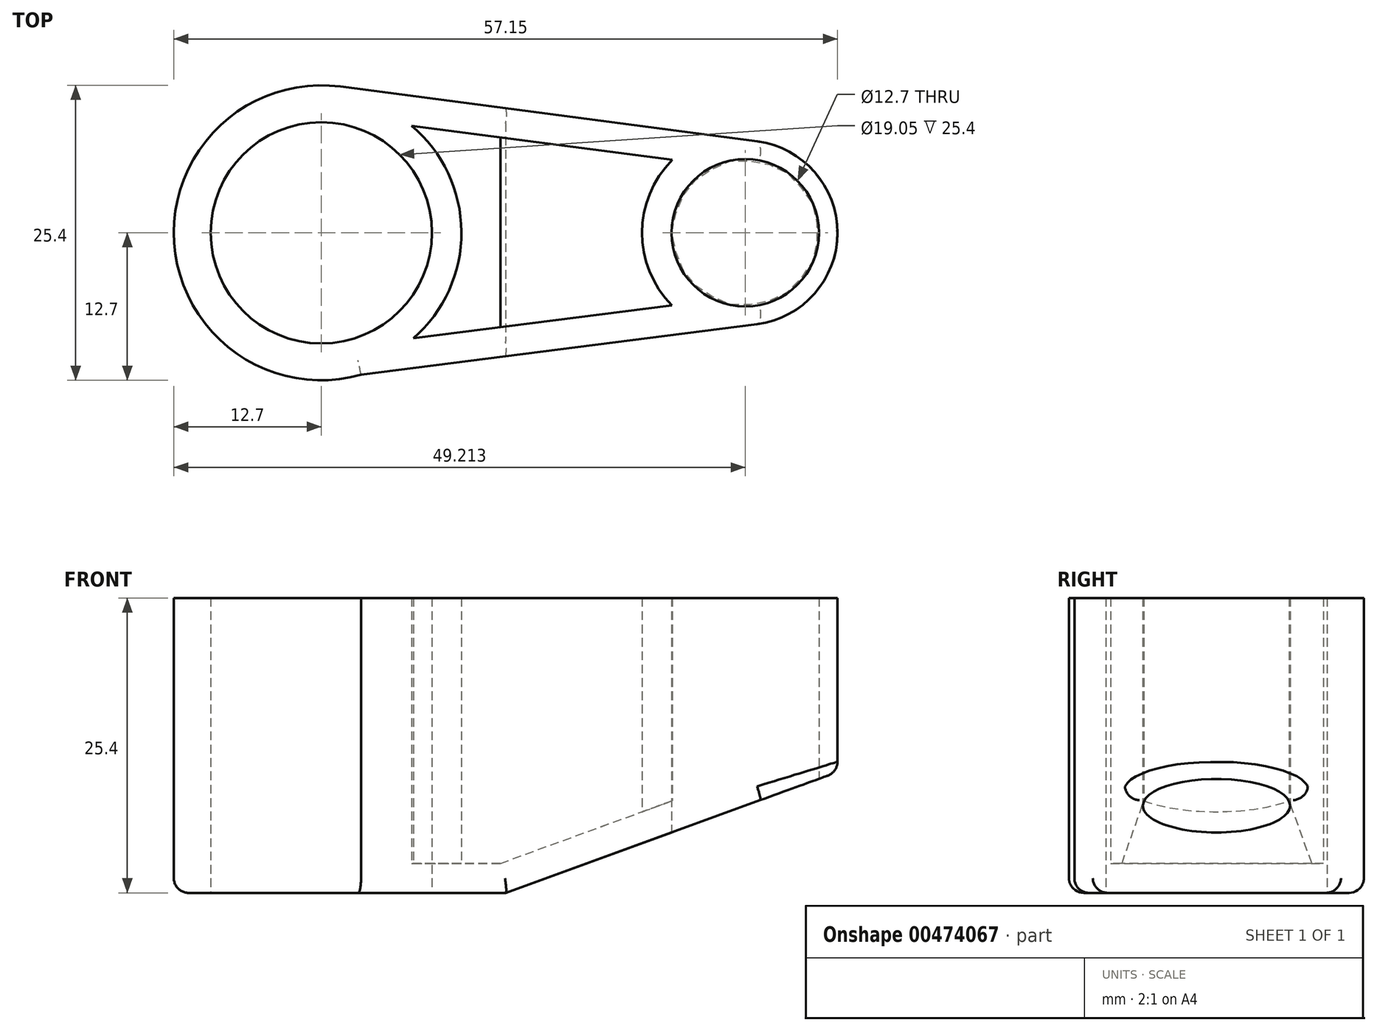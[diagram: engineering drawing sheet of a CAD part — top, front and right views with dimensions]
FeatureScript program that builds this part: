
annotation { "Feature Type Name" : "Feature", "Feature Type Description" : "" }
export const myFeature = defineFeature(function(context is Context, id is Id, definition is map)
    precondition{}
    {
        {
            var Q0;
            Q0=qCreatedBy(makeId("Top.planeOp"),FACE);
            var sketch = newSketch(context, id + "F0", { "sketchPlane" : qUnion([Q0])});
            skCircle(sketch, "E0", {"center": v(0, 0) * mm, "radius": 12.7 * mm});
            skCircle(sketch, "E1", {"center": v(36.51, 0) * mm, "radius": 7.94 * mm});
            skCircle(sketch, "E2", {"center": v(0, 0) * mm, "radius": 9.53 * mm});
            skCircle(sketch, "E3", {"center": v(36.51, 0) * mm, "radius": 6.35 * mm});
            skLineSegment(sketch, "E4", {"start": v(3.42, -12.23) * mm, "end": v(37.52, -7.87) * mm});
            skLineSegment(sketch, "E5", {"start": v(1.66, 12.6) * mm, "end": v(37.55, 7.87) * mm});
            skSolve(sketch);
        }
        {
            var Q0;
            {var subQ0=sQuery(id+"F0.wireOp",EDGE,"E4");Q0=makeQuery(id+"F0.imprint","IMPRINT",FACE,{"disambiguationData":[TD([[makeQuery(id+"F0.imprint","IMPRINT",EDGE,{"derivedFrom":subQ0}),1.0]])]});}
            var Q1;
            Q1=makeQuery(id+"F0.imprint","IMPRINT",FACE,{"disambiguationData":[TD([[makeQuery(id+"F0.imprint","IMPRINT",EDGE,{"derivedFrom":sQuery(id+"F0.wireOp",EDGE,"E2")}),-1.0]])]});
            var Q2;
            Q2=makeQuery(id+"F0.imprint","IMPRINT",FACE,{"disambiguationData":[TD([[makeQuery(id+"F0.imprint","IMPRINT",EDGE,{"derivedFrom":sQuery(id+"F0.wireOp",EDGE,"E3")}),-1.0]])]});
            extrude(context, id + "F1", {"entities" : qUnion([Q0, Q1, Q2]), "depth" : 25.4 * mm, "offsetDistance" : 25.4 * mm});
        }
        {
            var Q0;
            Q0=qCreatedBy(makeId("Front.planeOp"),FACE);
            var sketch = newSketch(context, id + "F2", { "sketchPlane" : qUnion([Q0])});
            skLineSegment(sketch, "E6", {"start": v(15.87, 0) * mm, "end": v(44.45, 10.4) * mm});
            skLineSegment(sketch, "E7", {"start": v(44.45, 10.4) * mm, "end": v(44.45, 0) * mm});
            skLineSegment(sketch, "E8", {"start": v(44.45, 0) * mm, "end": v(15.88, 0) * mm});
            skLineSegment(sketch, "E9", {"start": v(44.45, 25.4) * mm, "end": v(44.45, 0) * mm});
            skSolve(sketch);
        }
        {
            var Q0;
            Q0=makeQuery(id+"F2.imprint","IMPRINT",FACE,{"disambiguationData":[TD([[makeQuery(id+"F2.imprint","IMPRINT",EDGE,{"derivedFrom":sQuery(id+"F2.wireOp",EDGE,"E6")}),-1.0]])]});
            extrude(context, id + "F3", {"entities" : qUnion([Q0]), "operationType" : NewBodyOperationType.REMOVE, "oppositeDirection" : true, "depth" : 25.4 * mm, "offsetDistance" : 25.4 * mm, "hasSecondDirection" : true, "secondDirectionOppositeDirection" : false, "secondDirectionDepth" : 25.4 * mm});
        }
        {
            var Q0;
            Q0=makeQuery(id+"F3.boolean.opBoolean","INTERSECT",EDGE,{"derivedFrom":[makeQuery(id+"F1.opExtrude","SWEPT_FACE",FACE,{"disambiguationData":[OSD([sQuery(id+"F0.wireOp",EDGE,"E5")])]}),makeQuery(id+"F3.opExtrude","SWEPT_FACE",FACE,{"disambiguationData":[OSD([sQuery(id+"F2.wireOp",EDGE,"E6")])]})]});
            var Q1;
            Q1=makeQuery(id+"F1.opExtrude","CAP_EDGE",EDGE,{"disambiguationData":[OSD([sQuery(id+"F0.wireOp",EDGE,"E0")])],"isStart":true});
            var Q2;
            Q2=makeQuery(id+"F1.opExtrude","CAP_EDGE",EDGE,{"disambiguationData":[OSD([sQuery(id+"F0.wireOp",EDGE,"E5")])],"isStart":true});
            var Q3;
            Q3=makeQuery(id+"F1.opExtrude","CAP_EDGE",EDGE,{"disambiguationData":[OSD([sQuery(id+"F0.wireOp",EDGE,"E4")])],"isStart":true});
            var Q4;
            Q4=makeQuery(id+"F3.boolean.opBoolean","COPY",EDGE,{"derivedFrom":makeQuery(id+"F3.opExtrude","SWEPT_EDGE",EDGE,{"disambiguationData":[OSD([sQuery(id+"F2.wireOp",EDGE,"E6"),sQuery(id+"F2.wireOp",EDGE,"E8")])]})});
            fillet(context, id + "F4", {"entities" : qUnion([Q0, Q1, Q2, Q3, Q4]), "radius" : 1.27 * mm, "tangentPropagation" : true, "allowEdgeOverflow" : false});
        }
        {
            var Q0;
            Q0=makeQuery(id+"F1.opExtrude","CAP_FACE",FACE,{"disambiguationData":[OSD([sQuery(id+"F0.wireOp",EDGE,"E0"),sQuery(id+"F0.wireOp",EDGE,"E1"),sQuery(id+"F0.wireOp",EDGE,"E2"),sQuery(id+"F0.wireOp",EDGE,"E3"),sQuery(id+"F0.wireOp",EDGE,"E4"),sQuery(id+"F0.wireOp",EDGE,"E5")])],"isStart":false});
            shell(context, id + "F5", {"entities" : qUnion([Q0]), "thickness" : 2.54 * mm});
        }
    });
